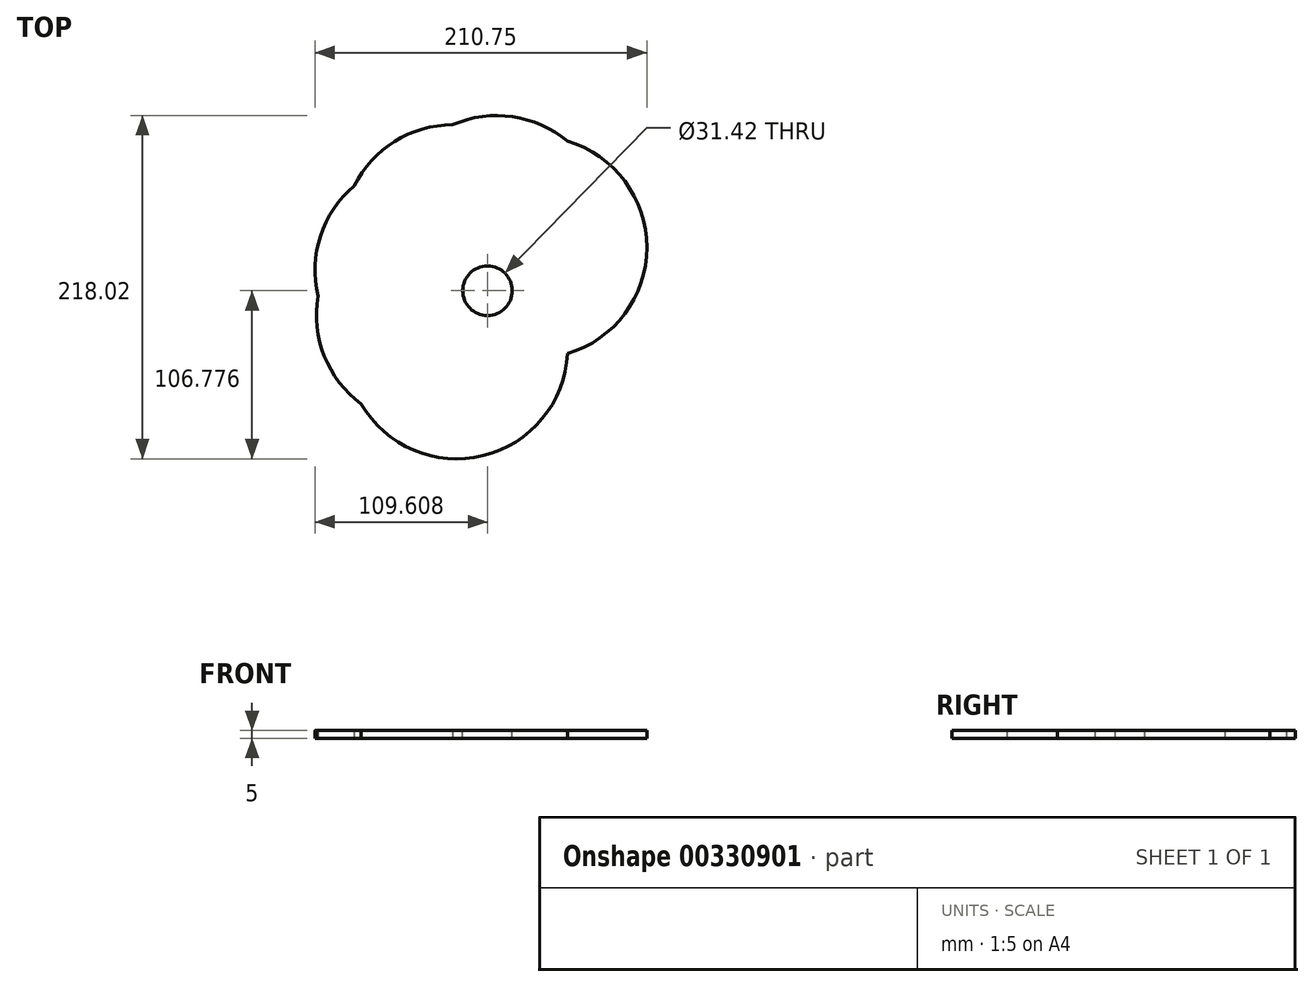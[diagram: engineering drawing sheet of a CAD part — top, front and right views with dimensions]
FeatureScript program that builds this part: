
annotation { "Feature Type Name" : "Feature", "Feature Type Description" : "" }
export const myFeature = defineFeature(function(context is Context, id is Id, definition is map)
    precondition{}
    {
        {
            var Q0;
            Q0=qCreatedBy(makeId("Top.planeOp"),FACE);
            var sketch = newSketch(context, id + "F0", { "sketchPlane" : qUnion([Q0])});
            skCircle(sketch, "E0", {"center": v(0, 0) * mm, "radius": 70.41 * mm});
            skSolve(sketch);
        }
        {
            var Q0;
            Q0=makeQuery(id+"F0.imprint","IMPRINT",FACE,{"disambiguationData":[TD([[makeQuery(id+"F0.imprint","IMPRINT",EDGE,{"derivedFrom":sQuery(id+"F0.wireOp",EDGE,"E0")}),1.0]])]});
            extrude(context, id + "F1", {"entities" : qUnion([Q0]), "depth" : 5 * mm});
        }
        {
            var Q0;
            Q0=makeQuery(id+"F1.opExtrude","CAP_FACE",FACE,{"disambiguationData":[OSD([sQuery(id+"F0.wireOp",EDGE,"E0")])],"isStart":false});
            var sketch = newSketch(context, id + "F2", { "sketchPlane" : qUnion([Q0])});
            skPoint(sketch, "E1", {"position": v(-30.73, -27.51) * mm});
            skCircle(sketch, "E2", {"center": v(-30.73, -27.51) * mm, "radius": 15.7 * mm});
            skSolve(sketch);
        }
        {
            var Q0;
            Q0 = qSketchRegion(id + "F2", true);
            extrude(context, id + "F3", {"entities" : qUnion([Q0]), "operationType" : NewBodyOperationType.REMOVE, "endBound" : BoundingType.THROUGH_ALL, "oppositeDirection" : true, "depth" : 25 * mm});
        }
        {
            var Q0;
            Q0=makeQuery(id+"F1.opExtrude","SWEPT_BODY",BODY,{"disambiguationData":[OSD([sQuery(id+"F0.wireOp",EDGE,"E0")])]});
            var Q1;
            Q1=makeQuery(id+"F3.boolean.opBoolean","INTERSECT",EDGE,{"derivedFrom":[makeQuery(id+"F1.opExtrude","CAP_FACE",FACE,{"disambiguationData":[OSD([sQuery(id+"F0.wireOp",EDGE,"E0")])],"isStart":true}),makeQuery(id+"F3.opExtrude","SWEPT_FACE",FACE,{"disambiguationData":[OSD([sQuery(id+"F2.wireOp",EDGE,"E2")])]})]});
            circularPattern(context, id + "F4", {"operationType" : NewBodyOperationType.ADD, "entities" : qUnion([Q0]), "axis" : qUnion([Q1]), "angle" : 200 * degree, "instanceCount" : 6, "equalSpace" : true});
        }
    });
